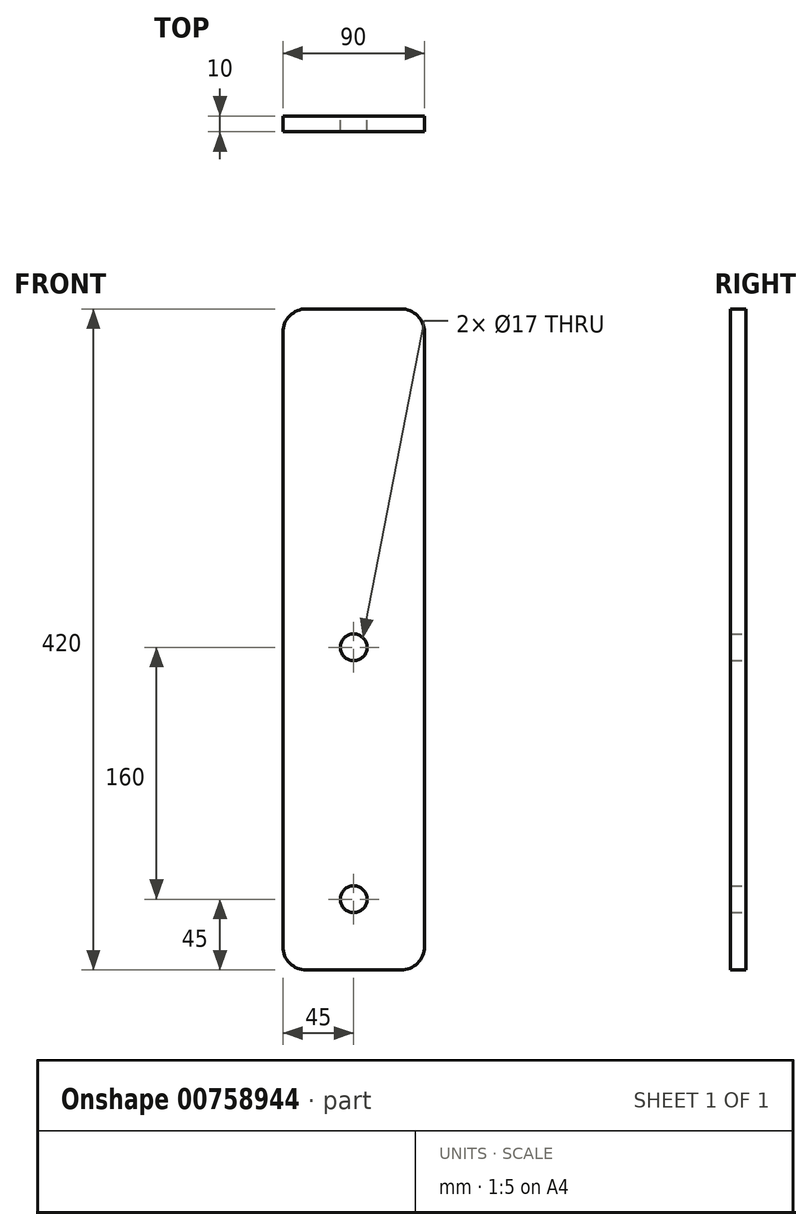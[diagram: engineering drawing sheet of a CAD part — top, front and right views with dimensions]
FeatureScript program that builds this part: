
annotation { "Feature Type Name" : "Feature", "Feature Type Description" : "" }
export const myFeature = defineFeature(function(context is Context, id is Id, definition is map)
    precondition{}
    {
        {
            var Q0;
            Q0=qCreatedBy(makeId("Front.planeOp"),FACE);
            var sketch = newSketch(context, id + "F0", { "sketchPlane" : qUnion([Q0])});
            skLineSegment(sketch, "E0.bottom", {"start": v(15, 0) * mm, "end": v(75, 0) * mm});
            skLineSegment(sketch, "E0.top", {"start": v(15, 420) * mm, "end": v(75, 420) * mm});
            skLineSegment(sketch, "E0.left", {"start": v(0, 15) * mm, "end": v(0, 405) * mm});
            skLineSegment(sketch, "E0.right", {"start": v(90, 15) * mm, "end": v(90, 405) * mm});
            skCircle(sketch, "E1", {"center": v(45, 205) * mm, "radius": 8.5 * mm});
            skCircle(sketch, "E2", {"center": v(45, 45) * mm, "radius": 8.5 * mm});
            skPoint(sketch, "E3.visualSharp", {"position": v(0, 420) * mm});
            skArc(sketch, "E3.filletArc", {"start": v(15, 420) * mm, "mid": v(4.4, 415.6) * mm, "end": v(0, 405) * mm});
            skPoint(sketch, "E4.visualSharp", {"position": v(90, 420) * mm});
            skArc(sketch, "E4.filletArc", {"start": v(90, 405) * mm, "mid": v(85.6, 415.6) * mm, "end": v(75, 420) * mm});
            skPoint(sketch, "E5.visualSharp", {"position": v(90, 0) * mm});
            skArc(sketch, "E5.filletArc", {"start": v(75, 0) * mm, "mid": v(85.6, 4.4) * mm, "end": v(90, 15) * mm});
            skPoint(sketch, "E6.visualSharp", {"position": v(0, 0) * mm});
            skArc(sketch, "E6.filletArc", {"start": v(0, 15) * mm, "mid": v(4.4, 4.4) * mm, "end": v(15, 0) * mm});
            skSolve(sketch);
        }
        {
            var Q0;
            Q0=makeQuery(id+"F0.imprint","IMPRINT",FACE,{"disambiguationData":[TD([[makeQuery(id+"F0.imprint","IMPRINT",EDGE,{"derivedFrom":sQuery(id+"F0.wireOp",EDGE,"E0.bottom")}),1.0]])]});
            extrude(context, id + "F1", {"entities" : qUnion([Q0]), "depth" : 10 * mm, "offsetDistance" : 25 * mm});
        }
    });
